FCSTD DOCUMENT  (FreeCAD 0.18R4 (GitTag))
Label: butelka front
License: All rights reserved
LicenseURL: http://en.wikipedia.org/wiki/All_rights_reserved
objects: Sketcher::SketchObject×1, PartDesign::Body×1
note: 2 computed .brp shape members not serialized (recipe doc carries the construction recipe); baked Part::Feature solids carry a one-line shape summary decoded from their .brp

FEATURE [Sketcher::SketchObject] Sketch
  MapMode = 5
  Support = -> [XY_Plane]
  sketch-geometry (321):
    g0: ArcOfCircle CenterX=0 CenterY=58.4018 CenterZ=0 NormalX=0 NormalY=0 NormalZ=1 AngleXU=0 Radius=67 StartAngle=2.08563 EndAngle=4.20019
    g1: LineSegment StartX=-17 StartY=149 StartZ=0 EndX=-16 EndY=149 EndZ=0
    g2: LineSegment StartX=17 StartY=149 StartZ=0 EndX=17 EndY=144.134 EndZ=0
    g3: LineSegment StartX=-17 StartY=144.134 StartZ=0 EndX=-17 EndY=149 EndZ=0
    g4: LineSegment [constr] StartX=-50 StartY=103 StartZ=0 EndX=50 EndY=103 EndZ=0
    g5: LineSegment StartX=32.8364 StartY=0 StartZ=0 EndX=-32.8364 EndY=7.1e-15 EndZ=0
    g6: ArcOfCircle CenterX=0 CenterY=58.4018 CenterZ=0 NormalX=0 NormalY=0 NormalZ=1 AngleXU=0 Radius=67 StartAngle=5.22459 EndAngle=7.33915
    g7: ArcOfCircle CenterX=48.5 CenterY=144.134 CenterZ=0 NormalX=0 NormalY=0 NormalZ=1 AngleXU=0 Radius=31.5 StartAngle=3.14159 EndAngle=4.19756
    g8: ArcOfCircle CenterX=-48.5 CenterY=144.134 CenterZ=0 NormalX=0 NormalY=0 NormalZ=1 AngleXU=0 Radius=31.5 StartAngle=5.22722 EndAngle=6.28319
    g9: LineSegment StartX=-16 StartY=211 StartZ=0 EndX=16 EndY=211 EndZ=0
    g10: LineSegment StartX=16 StartY=211 StartZ=0 EndX=16 EndY=149 EndZ=0
    g11: LineSegment StartX=-16 StartY=149 StartZ=0 EndX=-16 EndY=211 EndZ=0
    g12: LineSegment StartX=16 StartY=149 StartZ=0 EndX=17 EndY=149 EndZ=0
    g13: LineSegment StartX=-80 StartY=-15 StartZ=0 EndX=80 EndY=-15 EndZ=0
    g14: LineSegment StartX=80 StartY=-15 StartZ=0 EndX=80 EndY=10 EndZ=0
    g15: LineSegment StartX=80 StartY=10 StartZ=0 EndX=76.35 EndY=10 EndZ=0
    g16: LineSegment StartX=76.35 StartY=10 StartZ=0 EndX=76.35 EndY=13 EndZ=0
    g17: LineSegment StartX=76.35 StartY=13 StartZ=0 EndX=80 EndY=13 EndZ=0
    g18: LineSegment StartX=80 StartY=13 StartZ=0 EndX=80 EndY=16 EndZ=0
    g19: LineSegment StartX=80 StartY=16 StartZ=0 EndX=76.35 EndY=16 EndZ=0
    g20: LineSegment StartX=76.35 StartY=16 StartZ=0 EndX=76.35 EndY=19 EndZ=0
    g21: LineSegment StartX=76.35 StartY=19 StartZ=0 EndX=80 EndY=19 EndZ=0
    g22: LineSegment StartX=80 StartY=19 StartZ=0 EndX=80 EndY=22 EndZ=0
    g23: LineSegment StartX=80 StartY=22 StartZ=0 EndX=76.35 EndY=22 EndZ=0
    g24: LineSegment StartX=76.35 StartY=22 StartZ=0 EndX=76.35 EndY=25 EndZ=0
    g25: LineSegment StartX=76.35 StartY=25 StartZ=0 EndX=80 EndY=25 EndZ=0
    g26: LineSegment StartX=80 StartY=25 StartZ=0 EndX=80 EndY=28 EndZ=0
    g27: LineSegment StartX=80 StartY=28 StartZ=0 EndX=76.35 EndY=28 EndZ=0
    g28: LineSegment StartX=76.35 StartY=28 StartZ=0 EndX=76.35 EndY=31 EndZ=0
    g29: LineSegment StartX=76.35 StartY=31 StartZ=0 EndX=80 EndY=31 EndZ=0
    g30: LineSegment StartX=80 StartY=31 StartZ=0 EndX=80 EndY=34 EndZ=0
    g31: LineSegment StartX=80 StartY=34 StartZ=0 EndX=76.35 EndY=34 EndZ=0
    g32: LineSegment StartX=76.35 StartY=34 StartZ=0 EndX=76.35 EndY=37 EndZ=0
    g33: LineSegment StartX=76.35 StartY=37 StartZ=0 EndX=80 EndY=37 EndZ=0
    g34: LineSegment StartX=80 StartY=37 StartZ=0 EndX=80 EndY=40 EndZ=0
    g35: LineSegment StartX=80 StartY=40 StartZ=0 EndX=76.35 EndY=40 EndZ=0
    g36: LineSegment StartX=76.35 StartY=40 StartZ=0 EndX=76.35 EndY=43 EndZ=0
    g37: LineSegment StartX=76.35 StartY=43 StartZ=0 EndX=80 EndY=43 EndZ=0
    g38: LineSegment StartX=80 StartY=43 StartZ=0 EndX=80 EndY=46 EndZ=0
    g39: LineSegment StartX=80 StartY=46 StartZ=0 EndX=76.35 EndY=46 EndZ=0
    g40: LineSegment StartX=76.35 StartY=46 StartZ=0 EndX=76.35 EndY=49 EndZ=0
    g41: LineSegment StartX=76.35 StartY=49 StartZ=0 EndX=80 EndY=49 EndZ=0
    g42: LineSegment StartX=80 StartY=49 StartZ=0 EndX=80 EndY=52 EndZ=0
    g43: LineSegment StartX=80 StartY=52 StartZ=0 EndX=76.35 EndY=52 EndZ=0
    g44: LineSegment StartX=76.35 StartY=52 StartZ=0 EndX=76.35 EndY=55 EndZ=0
    g45: LineSegment StartX=76.35 StartY=55 StartZ=0 EndX=80 EndY=55 EndZ=0
    g46: LineSegment StartX=80 StartY=55 StartZ=0 EndX=80 EndY=58 EndZ=0
    g47: LineSegment StartX=80 StartY=58 StartZ=0 EndX=76.35 EndY=58 EndZ=0
    g48: LineSegment StartX=76.35 StartY=58 StartZ=0 EndX=76.35 EndY=61 EndZ=0
    g49: LineSegment StartX=76.35 StartY=61 StartZ=0 EndX=80 EndY=61 EndZ=0
    g50: LineSegment StartX=80 StartY=61 StartZ=0 EndX=80 EndY=64 EndZ=0
    g51: LineSegment StartX=80 StartY=64 StartZ=0 EndX=76.35 EndY=64 EndZ=0
    g52: LineSegment StartX=76.35 StartY=64 StartZ=0 EndX=76.35 EndY=67 EndZ=0
    g53: LineSegment StartX=76.35 StartY=67 StartZ=0 EndX=80 EndY=67 EndZ=0
    g54: LineSegment StartX=80 StartY=67 StartZ=0 EndX=80 EndY=70 EndZ=0
    g55: LineSegment StartX=80 StartY=70 StartZ=0 EndX=76.35 EndY=70 EndZ=0
    g56: LineSegment StartX=76.35 StartY=70 StartZ=0 EndX=76.35 EndY=73 EndZ=0
    g57: LineSegment StartX=76.35 StartY=73 StartZ=0 EndX=80 EndY=73 EndZ=0
    g58: LineSegment StartX=80 StartY=73 StartZ=0 EndX=80 EndY=76 EndZ=0
    g59: LineSegment StartX=80 StartY=76 StartZ=0 EndX=76.35 EndY=76 EndZ=0
    g60: LineSegment StartX=76.35 StartY=76 StartZ=0 EndX=76.35 EndY=79 EndZ=0
    g61: LineSegment StartX=76.35 StartY=79 StartZ=0 EndX=80 EndY=79 EndZ=0
    g62: LineSegment StartX=80 StartY=79 StartZ=0 EndX=80 EndY=82 EndZ=0
    g63: LineSegment StartX=80 StartY=82 StartZ=0 EndX=76.35 EndY=82 EndZ=0
    g64: LineSegment StartX=76.35 StartY=82 StartZ=0 EndX=76.35 EndY=85 EndZ=0
    g65: LineSegment StartX=76.35 StartY=85 StartZ=0 EndX=80 EndY=85 EndZ=0
    g66: LineSegment StartX=80 StartY=85 StartZ=0 EndX=80 EndY=88 EndZ=0
    g67: LineSegment StartX=80 StartY=88 StartZ=0 EndX=76.35 EndY=88 EndZ=0
    g68: LineSegment StartX=76.35 StartY=88 StartZ=0 EndX=76.35 EndY=91 EndZ=0
    g69: LineSegment StartX=76.35 StartY=91 StartZ=0 EndX=80 EndY=91 EndZ=0
    g70: LineSegment StartX=80 StartY=91 StartZ=0 EndX=80 EndY=94 EndZ=0
    g71: LineSegment StartX=80 StartY=94 StartZ=0 EndX=76.35 EndY=94 EndZ=0
    g72: LineSegment StartX=76.35 StartY=94 StartZ=0 EndX=76.35 EndY=97 EndZ=0
    g73: LineSegment StartX=76.35 StartY=97 StartZ=0 EndX=80 EndY=97 EndZ=0
    g74: LineSegment StartX=80 StartY=97 StartZ=0 EndX=80 EndY=100 EndZ=0
    g75: LineSegment StartX=80 StartY=100 StartZ=0 EndX=76.35 EndY=100 EndZ=0
    g76: LineSegment StartX=76.35 StartY=100 StartZ=0 EndX=76.35 EndY=103 EndZ=0
    g77: LineSegment StartX=76.35 StartY=103 StartZ=0 EndX=80 EndY=103 EndZ=0
    g78: LineSegment StartX=80 StartY=103 StartZ=0 EndX=80 EndY=106 EndZ=0
    g79: LineSegment StartX=80 StartY=106 StartZ=0 EndX=76.35 EndY=106 EndZ=0
    g80: LineSegment StartX=76.35 StartY=106 StartZ=0 EndX=76.35 EndY=109 EndZ=0
    g81: LineSegment StartX=76.35 StartY=109 StartZ=0 EndX=80 EndY=109 EndZ=0
    g82: LineSegment StartX=80 StartY=109 StartZ=0 EndX=80 EndY=112 EndZ=0
    g83: LineSegment StartX=80 StartY=112 StartZ=0 EndX=76.35 EndY=112 EndZ=0
    g84: LineSegment StartX=76.35 StartY=112 StartZ=0 EndX=76.35 EndY=115 EndZ=0
    g85: LineSegment StartX=76.35 StartY=115 StartZ=0 EndX=80 EndY=115 EndZ=0
    g86: LineSegment StartX=80 StartY=115 StartZ=0 EndX=80 EndY=118 EndZ=0
    g87: LineSegment StartX=80 StartY=118 StartZ=0 EndX=76.35 EndY=118 EndZ=0
    g88: LineSegment StartX=76.35 StartY=118 StartZ=0 EndX=76.35 EndY=121 EndZ=0
    g89: LineSegment StartX=76.35 StartY=121 StartZ=0 EndX=80 EndY=121 EndZ=0
    g90: LineSegment StartX=80 StartY=121 StartZ=0 EndX=80 EndY=124 EndZ=0
    g91: LineSegment StartX=80 StartY=124 StartZ=0 EndX=76.35 EndY=124 EndZ=0
    g92: LineSegment StartX=76.35 StartY=124 StartZ=0 EndX=76.35 EndY=127 EndZ=0
    g93: LineSegment StartX=76.35 StartY=127 StartZ=0 EndX=80 EndY=127 EndZ=0
    g94: LineSegment StartX=80 StartY=127 StartZ=0 EndX=80 EndY=130 EndZ=0
    g95: LineSegment StartX=80 StartY=130 StartZ=0 EndX=76.35 EndY=130 EndZ=0
    g96: LineSegment StartX=76.35 StartY=130 StartZ=0 EndX=76.35 EndY=133 EndZ=0
    g97: LineSegment StartX=76.35 StartY=133 StartZ=0 EndX=80 EndY=133 EndZ=0
    g98: LineSegment StartX=80 StartY=133 StartZ=0 EndX=80 EndY=136 EndZ=0
    g99: LineSegment StartX=80 StartY=136 StartZ=0 EndX=76.35 EndY=136 EndZ=0
    g100: LineSegment StartX=76.35 StartY=136 StartZ=0 EndX=76.35 EndY=139 EndZ=0
    g101: LineSegment StartX=76.35 StartY=139 StartZ=0 EndX=80 EndY=139 EndZ=0
    g102: LineSegment StartX=80 StartY=139 StartZ=0 EndX=80 EndY=142 EndZ=0
    g103: LineSegment StartX=80 StartY=142 StartZ=0 EndX=76.35 EndY=142 EndZ=0
    g104: LineSegment StartX=76.35 StartY=142 StartZ=0 EndX=76.35 EndY=145 EndZ=0
    g105: LineSegment StartX=76.35 StartY=145 StartZ=0 EndX=80 EndY=145 EndZ=0
    g106: LineSegment StartX=80 StartY=145 StartZ=0 EndX=80 EndY=148 EndZ=0
    g107: LineSegment StartX=80 StartY=148 StartZ=0 EndX=76.35 EndY=148 EndZ=0
    g108: LineSegment StartX=76.35 StartY=148 StartZ=0 EndX=76.35 EndY=151 EndZ=0
    g109: LineSegment StartX=76.35 StartY=151 StartZ=0 EndX=80 EndY=151 EndZ=0
    g110: LineSegment StartX=80 StartY=151 StartZ=0 EndX=80 EndY=154 EndZ=0
    g111: LineSegment StartX=80 StartY=154 StartZ=0 EndX=76.35 EndY=154 EndZ=0
    g112: LineSegment StartX=76.35 StartY=154 StartZ=0 EndX=76.35 EndY=157 EndZ=0
    g113: LineSegment StartX=76.35 StartY=157 StartZ=0 EndX=80 EndY=157 EndZ=0
    g114: LineSegment StartX=80 StartY=157 StartZ=0 EndX=80 EndY=160 EndZ=0
    g115: LineSegment StartX=80 StartY=160 StartZ=0 EndX=76.35 EndY=160 EndZ=0
    g116: LineSegment StartX=76.35 StartY=160 StartZ=0 EndX=76.35 EndY=163 EndZ=0
    g117: LineSegment StartX=76.35 StartY=163 StartZ=0 EndX=80 EndY=163 EndZ=0
    g118: LineSegment StartX=80 StartY=163 StartZ=0 EndX=80 EndY=166 EndZ=0
    g119: LineSegment StartX=80 StartY=166 StartZ=0 EndX=76.35 EndY=166 EndZ=0
    g120: LineSegment StartX=76.35 StartY=166 StartZ=0 EndX=76.35 EndY=169 EndZ=0
    g121: LineSegment StartX=76.35 StartY=169 StartZ=0 EndX=80 EndY=169 EndZ=0
    g122: LineSegment StartX=80 StartY=169 StartZ=0 EndX=80 EndY=172 EndZ=0
    g123: LineSegment StartX=80 StartY=172 StartZ=0 EndX=76.35 EndY=172 EndZ=0
    g124: LineSegment StartX=76.35 StartY=172 StartZ=0 EndX=76.35 EndY=175 EndZ=0
    g125: LineSegment StartX=76.35 StartY=175 StartZ=0 EndX=80 EndY=175 EndZ=0
    g126: LineSegment StartX=80 StartY=175 StartZ=0 EndX=80 EndY=178 EndZ=0
    g127: LineSegment StartX=80 StartY=178 StartZ=0 EndX=76.35 EndY=178 EndZ=0
    g128: LineSegment StartX=76.35 StartY=178 StartZ=0 EndX=76.35 EndY=181 EndZ=0
    g129: LineSegment StartX=76.35 StartY=181 StartZ=0 EndX=80 EndY=181 EndZ=0
    g130: LineSegment StartX=80 StartY=181 StartZ=0 EndX=80 EndY=184 EndZ=0
    g131: LineSegment StartX=80 StartY=184 StartZ=0 EndX=76.35 EndY=184 EndZ=0
    g132: LineSegment StartX=76.35 StartY=184 StartZ=0 EndX=76.35 EndY=187 EndZ=0
    g133: LineSegment StartX=76.35 StartY=187 StartZ=0 EndX=80 EndY=187 EndZ=0
    g134: LineSegment StartX=80 StartY=187 StartZ=0 EndX=80 EndY=190 EndZ=0
    g135: LineSegment StartX=80 StartY=190 StartZ=0 EndX=76.35 EndY=190 EndZ=0
    g136: LineSegment StartX=76.35 StartY=190 StartZ=0 EndX=76.35 EndY=193 EndZ=0
    g137: LineSegment StartX=76.35 StartY=193 StartZ=0 EndX=80 EndY=193 EndZ=0
    g138: LineSegment StartX=80 StartY=193 StartZ=0 EndX=80 EndY=196 EndZ=0
    g139: LineSegment StartX=80 StartY=196 StartZ=0 EndX=76.35 EndY=196 EndZ=0
    g140: LineSegment StartX=76.35 StartY=196 StartZ=0 EndX=76.35 EndY=199 EndZ=0
    g141: LineSegment StartX=76.35 StartY=199 StartZ=0 EndX=80 EndY=199 EndZ=0
    g142: LineSegment StartX=80 StartY=199 StartZ=0 EndX=80 EndY=202 EndZ=0
    g143: LineSegment StartX=80 StartY=202 StartZ=0 EndX=76.35 EndY=202 EndZ=0
    g144: LineSegment StartX=76.35 StartY=202 StartZ=0 EndX=76.35 EndY=205 EndZ=0
    g145: LineSegment StartX=76.35 StartY=205 StartZ=0 EndX=80 EndY=205 EndZ=0
    g146: LineSegment StartX=80 StartY=205 StartZ=0 EndX=80 EndY=208 EndZ=0
    g147: LineSegment StartX=80 StartY=208 StartZ=0 EndX=76.35 EndY=208 EndZ=0
    g148: LineSegment StartX=76.35 StartY=208 StartZ=0 EndX=76.35 EndY=211 EndZ=0
    g149: LineSegment StartX=76.35 StartY=211 StartZ=0 EndX=80 EndY=211 EndZ=0
    g150: LineSegment StartX=80 StartY=211 StartZ=0 EndX=80 EndY=214 EndZ=0
    g151: LineSegment StartX=80 StartY=214 StartZ=0 EndX=76.35 EndY=214 EndZ=0
    g152: LineSegment StartX=76.35 StartY=214 StartZ=0 EndX=76.35 EndY=217 EndZ=0
    g153: LineSegment StartX=76.35 StartY=217 StartZ=0 EndX=80 EndY=217 EndZ=0
    g154: LineSegment StartX=80 StartY=217 StartZ=0 EndX=80 EndY=220 EndZ=0
    g155: LineSegment StartX=80 StartY=220 StartZ=0 EndX=76.35 EndY=220 EndZ=0
    g156: LineSegment StartX=76.35 StartY=220 StartZ=0 EndX=76.35 EndY=223 EndZ=0
    g157: LineSegment StartX=76.35 StartY=223 StartZ=0 EndX=80 EndY=223 EndZ=0
    g158: LineSegment StartX=80 StartY=223 StartZ=0 EndX=80 EndY=226 EndZ=0
    g159: LineSegment StartX=80 StartY=226 StartZ=0 EndX=76.35 EndY=226 EndZ=0
    g160: LineSegment StartX=76.35 StartY=226 StartZ=0 EndX=76.35 EndY=229 EndZ=0
    g161: LineSegment StartX=76.35 StartY=229 StartZ=0 EndX=80 EndY=229 EndZ=0
    g162: LineSegment StartX=80 StartY=229 StartZ=0 EndX=80 EndY=232 EndZ=0
    g163: LineSegment StartX=80 StartY=232 StartZ=0 EndX=76.35 EndY=232 EndZ=0
    g164: LineSegment StartX=76.35 StartY=232 StartZ=0 EndX=76.35 EndY=235 EndZ=0
    g165: LineSegment StartX=76.35 StartY=235 StartZ=0 EndX=80 EndY=235 EndZ=0
    g166: LineSegment StartX=80 StartY=235 StartZ=0 EndX=80 EndY=260 EndZ=0
    g167: LineSegment StartX=80 StartY=260 StartZ=0 EndX=-80 EndY=260 EndZ=0
    g168: LineSegment StartX=-80 StartY=260 StartZ=0 EndX=-80 EndY=235 EndZ=0
    g169: LineSegment StartX=-80 StartY=235 StartZ=0 EndX=-76.35 EndY=235 EndZ=0
    g170: LineSegment StartX=-76.35 StartY=235 StartZ=0 EndX=-76.35 EndY=232 EndZ=0
    g171: LineSegment StartX=-76.35 StartY=232 StartZ=0 EndX=-80 EndY=232 EndZ=0
    g172: LineSegment StartX=-80 StartY=232 StartZ=0 EndX=-80 EndY=229 EndZ=0
    g173: LineSegment StartX=-80 StartY=229 StartZ=0 EndX=-76.35 EndY=229 EndZ=0
    g174: LineSegment StartX=-76.35 StartY=229 StartZ=0 EndX=-76.35 EndY=226 EndZ=0
    g175: LineSegment StartX=-76.35 StartY=226 StartZ=0 EndX=-80 EndY=226 EndZ=0
    g176: LineSegment StartX=-80 StartY=226 StartZ=0 EndX=-80 EndY=223 EndZ=0
    g177: LineSegment StartX=-80 StartY=223 StartZ=0 EndX=-76.35 EndY=223 EndZ=0
    g178: LineSegment StartX=-76.35 StartY=223 StartZ=0 EndX=-76.35 EndY=220 EndZ=0
    g179: LineSegment StartX=-76.35 StartY=220 StartZ=0 EndX=-80 EndY=220 EndZ=0
    g180: LineSegment StartX=-80 StartY=220 StartZ=0 EndX=-80 EndY=217 EndZ=0
    g181: LineSegment StartX=-80 StartY=217 StartZ=0 EndX=-76.35 EndY=217 EndZ=0
    g182: LineSegment StartX=-76.35 StartY=217 StartZ=0 EndX=-76.35 EndY=214 EndZ=0
    g183: LineSegment StartX=-76.35 StartY=214 StartZ=0 EndX=-80 EndY=214 EndZ=0
    g184: LineSegment StartX=-80 StartY=214 StartZ=0 EndX=-80 EndY=211 EndZ=0
    g185: LineSegment StartX=-80 StartY=211 StartZ=0 EndX=-76.35 EndY=211 EndZ=0
    g186: LineSegment StartX=-76.35 StartY=211 StartZ=0 EndX=-76.35 EndY=208 EndZ=0
    g187: LineSegment StartX=-76.35 StartY=208 StartZ=0 EndX=-80 EndY=208 EndZ=0
    g188: LineSegment StartX=-80 StartY=208 StartZ=0 EndX=-80 EndY=205 EndZ=0
    g189: LineSegment StartX=-80 StartY=205 StartZ=0 EndX=-76.35 EndY=205 EndZ=0
    g190: LineSegment StartX=-76.35 StartY=205 StartZ=0 EndX=-76.35 EndY=202 EndZ=0
    g191: LineSegment StartX=-76.35 StartY=202 StartZ=0 EndX=-80 EndY=202 EndZ=0
    g192: LineSegment StartX=-80 StartY=202 StartZ=0 EndX=-80 EndY=199 EndZ=0
    g193: LineSegment StartX=-80 StartY=199 StartZ=0 EndX=-76.35 EndY=199 EndZ=0
    g194: LineSegment StartX=-76.35 StartY=199 StartZ=0 EndX=-76.35 EndY=196 EndZ=0
    g195: LineSegment StartX=-76.35 StartY=196 StartZ=0 EndX=-80 EndY=196 EndZ=0
    g196: LineSegment StartX=-80 StartY=196 StartZ=0 EndX=-80 EndY=193 EndZ=0
    g197: LineSegment StartX=-80 StartY=193 StartZ=0 EndX=-76.35 EndY=193 EndZ=0
    g198: LineSegment StartX=-76.35 StartY=193 StartZ=0 EndX=-76.35 EndY=190 EndZ=0
    g199: LineSegment StartX=-76.35 StartY=190 StartZ=0 EndX=-80 EndY=190 EndZ=0
    g200: LineSegment StartX=-80 StartY=190 StartZ=0 EndX=-80 EndY=187 EndZ=0
    g201: LineSegment StartX=-80 StartY=187 StartZ=0 EndX=-76.35 EndY=187 EndZ=0
    g202: LineSegment StartX=-76.35 StartY=187 StartZ=0 EndX=-76.35 EndY=184 EndZ=0
    g203: LineSegment StartX=-76.35 StartY=184 StartZ=0 EndX=-80 EndY=184 EndZ=0
    g204: LineSegment StartX=-80 StartY=184 StartZ=0 EndX=-80 EndY=181 EndZ=0
    g205: LineSegment StartX=-80 StartY=181 StartZ=0 EndX=-76.35 EndY=181 EndZ=0
    g206: LineSegment StartX=-76.35 StartY=181 StartZ=0 EndX=-76.35 EndY=178 EndZ=0
    g207: LineSegment StartX=-76.35 StartY=178 StartZ=0 EndX=-80 EndY=178 EndZ=0
    g208: LineSegment StartX=-80 StartY=178 StartZ=0 EndX=-80 EndY=175 EndZ=0
    g209: LineSegment StartX=-80 StartY=175 StartZ=0 EndX=-76.35 EndY=175 EndZ=0
    g210: LineSegment StartX=-76.35 StartY=175 StartZ=0 EndX=-76.35 EndY=172 EndZ=0
    g211: LineSegment StartX=-76.35 StartY=172 StartZ=0 EndX=-80 EndY=172 EndZ=0
    g212: LineSegment StartX=-80 StartY=172 StartZ=0 EndX=-80 EndY=169 EndZ=0
    g213: LineSegment StartX=-80 StartY=169 StartZ=0 EndX=-76.35 EndY=169 EndZ=0
    g214: LineSegment StartX=-76.35 StartY=169 StartZ=0 EndX=-76.35 EndY=166 EndZ=0
    g215: LineSegment StartX=-76.35 StartY=166 StartZ=0 EndX=-80 EndY=166 EndZ=0
    g216: LineSegment StartX=-80 StartY=166 StartZ=0 EndX=-80 EndY=163 EndZ=0
    g217: LineSegment StartX=-80 StartY=163 StartZ=0 EndX=-76.35 EndY=163 EndZ=0
    g218: LineSegment StartX=-76.35 StartY=163 StartZ=0 EndX=-76.35 EndY=160 EndZ=0
    g219: LineSegment StartX=-76.35 StartY=160 StartZ=0 EndX=-80 EndY=160 EndZ=0
    g220: LineSegment StartX=-80 StartY=160 StartZ=0 EndX=-80 EndY=157 EndZ=0
    g221: LineSegment StartX=-80 StartY=157 StartZ=0 EndX=-76.35 EndY=157 EndZ=0
    g222: LineSegment StartX=-76.35 StartY=157 StartZ=0 EndX=-76.35 EndY=154 EndZ=0
    g223: LineSegment StartX=-76.35 StartY=154 StartZ=0 EndX=-80 EndY=154 EndZ=0
    g224: LineSegment StartX=-80 StartY=154 StartZ=0 EndX=-80 EndY=151 EndZ=0
    g225: LineSegment StartX=-80 StartY=151 StartZ=0 EndX=-76.35 EndY=151 EndZ=0
    g226: LineSegment StartX=-76.35 StartY=151 StartZ=0 EndX=-76.35 EndY=148 EndZ=0
    g227: LineSegment StartX=-76.35 StartY=148 StartZ=0 EndX=-80 EndY=148 EndZ=0
    g228: LineSegment StartX=-80 StartY=148 StartZ=0 EndX=-80 EndY=145 EndZ=0
    g229: LineSegment StartX=-80 StartY=145 StartZ=0 EndX=-76.35 EndY=145 EndZ=0
    g230: LineSegment StartX=-76.35 StartY=145 StartZ=0 EndX=-76.35 EndY=142 EndZ=0
    g231: LineSegment StartX=-76.35 StartY=142 StartZ=0 EndX=-80 EndY=142 EndZ=0
    g232: LineSegment StartX=-80 StartY=142 StartZ=0 EndX=-80 EndY=139 EndZ=0
    g233: LineSegment StartX=-80 StartY=139 StartZ=0 EndX=-76.35 EndY=139 EndZ=0
    g234: LineSegment StartX=-76.35 StartY=139 StartZ=0 EndX=-76.35 EndY=136 EndZ=0
    g235: LineSegment StartX=-76.35 StartY=136 StartZ=0 EndX=-80 EndY=136 EndZ=0
    g236: LineSegment StartX=-80 StartY=136 StartZ=0 EndX=-80 EndY=133 EndZ=0
    g237: LineSegment StartX=-80 StartY=133 StartZ=0 EndX=-76.35 EndY=133 EndZ=0
    g238: LineSegment StartX=-76.35 StartY=133 StartZ=0 EndX=-76.35 EndY=130 EndZ=0
    g239: LineSegment StartX=-76.35 StartY=130 StartZ=0 EndX=-80 EndY=130 EndZ=0
    g240: LineSegment StartX=-80 StartY=130 StartZ=0 EndX=-80 EndY=127 EndZ=0
    g241: LineSegment StartX=-80 StartY=127 StartZ=0 EndX=-76.35 EndY=127 EndZ=0
    g242: LineSegment StartX=-76.35 StartY=127 StartZ=0 EndX=-76.35 EndY=124 EndZ=0
    g243: LineSegment StartX=-76.35 StartY=124 StartZ=0 EndX=-80 EndY=124 EndZ=0
    g244: LineSegment StartX=-80 StartY=124 StartZ=0 EndX=-80 EndY=121 EndZ=0
    g245: LineSegment StartX=-80 StartY=121 StartZ=0 EndX=-76.35 EndY=121 EndZ=0
    g246: LineSegment StartX=-76.35 StartY=121 StartZ=0 EndX=-76.35 EndY=118 EndZ=0
    g247: LineSegment StartX=-76.35 StartY=118 StartZ=0 EndX=-80 EndY=118 EndZ=0
    g248: LineSegment StartX=-80 StartY=118 StartZ=0 EndX=-80 EndY=115 EndZ=0
    g249: LineSegment StartX=-80 StartY=115 StartZ=0 EndX=-76.35 EndY=115 EndZ=0
    g250: LineSegment StartX=-76.35 StartY=115 StartZ=0 EndX=-76.35 EndY=112 EndZ=0
    g251: LineSegment StartX=-76.35 StartY=112 StartZ=0 EndX=-80 EndY=112 EndZ=0
    g252: LineSegment StartX=-80 StartY=112 StartZ=0 EndX=-80 EndY=109 EndZ=0
    g253: LineSegment StartX=-80 StartY=109 StartZ=0 EndX=-76.35 EndY=109 EndZ=0
    g254: LineSegment StartX=-76.35 StartY=109 StartZ=0 EndX=-76.35 EndY=106 EndZ=0
    g255: LineSegment StartX=-76.35 StartY=106 StartZ=0 EndX=-80 EndY=106 EndZ=0
    g256: LineSegment StartX=-80 StartY=106 StartZ=0 EndX=-80 EndY=103 EndZ=0
    g257: LineSegment StartX=-80 StartY=103 StartZ=0 EndX=-76.35 EndY=103 EndZ=0
    g258: LineSegment StartX=-76.35 StartY=103 StartZ=0 EndX=-76.35 EndY=100 EndZ=0
    g259: LineSegment StartX=-76.35 StartY=100 StartZ=0 EndX=-80 EndY=100 EndZ=0
    g260: LineSegment StartX=-80 StartY=100 StartZ=0 EndX=-80 EndY=97 EndZ=0
    g261: LineSegment StartX=-80 StartY=97 StartZ=0 EndX=-76.35 EndY=97 EndZ=0
    g262: LineSegment StartX=-76.35 StartY=97 StartZ=0 EndX=-76.35 EndY=94 EndZ=0
    g263: LineSegment StartX=-76.35 StartY=94 StartZ=0 EndX=-80 EndY=94 EndZ=0
    g264: LineSegment StartX=-80 StartY=94 StartZ=0 EndX=-80 EndY=91 EndZ=0
    g265: LineSegment StartX=-80 StartY=91 StartZ=0 EndX=-76.35 EndY=91 EndZ=0
    g266: LineSegment StartX=-76.35 StartY=91 StartZ=0 EndX=-76.35 EndY=88 EndZ=0
    g267: LineSegment StartX=-76.35 StartY=88 StartZ=0 EndX=-80 EndY=88 EndZ=0
    g268: LineSegment StartX=-80 StartY=88 StartZ=0 EndX=-80 EndY=85 EndZ=0
    g269: LineSegment StartX=-80 StartY=85 StartZ=0 EndX=-76.35 EndY=85 EndZ=0
    g270: LineSegment StartX=-76.35 StartY=85 StartZ=0 EndX=-76.35 EndY=82 EndZ=0
    g271: LineSegment StartX=-76.35 StartY=82 StartZ=0 EndX=-80 EndY=82 EndZ=0
    g272: LineSegment StartX=-80 StartY=82 StartZ=0 EndX=-80 EndY=79 EndZ=0
    g273: LineSegment StartX=-80 StartY=79 StartZ=0 EndX=-76.35 EndY=79 EndZ=0
    g274: LineSegment StartX=-76.35 StartY=79 StartZ=0 EndX=-76.35 EndY=76 EndZ=0
    g275: LineSegment StartX=-76.35 StartY=76 StartZ=0 EndX=-80 EndY=76 EndZ=0
    g276: LineSegment StartX=-80 StartY=76 StartZ=0 EndX=-80 EndY=73 EndZ=0
    g277: LineSegment StartX=-80 StartY=73 StartZ=0 EndX=-76.35 EndY=73 EndZ=0
    g278: LineSegment StartX=-76.35 StartY=73 StartZ=0 EndX=-76.35 EndY=70 EndZ=0
    g279: LineSegment StartX=-76.35 StartY=70 StartZ=0 EndX=-80 EndY=70 EndZ=0
    g280: LineSegment StartX=-80 StartY=70 StartZ=0 EndX=-80 EndY=67 EndZ=0
    g281: LineSegment StartX=-80 StartY=67 StartZ=0 EndX=-76.35 EndY=67 EndZ=0
    g282: LineSegment StartX=-76.35 StartY=67 StartZ=0 EndX=-76.35 EndY=64 EndZ=0
    g283: LineSegment StartX=-76.35 StartY=64 StartZ=0 EndX=-80 EndY=64 EndZ=0
    g284: LineSegment StartX=-80 StartY=64 StartZ=0 EndX=-80 EndY=61 EndZ=0
    g285: LineSegment StartX=-80 StartY=61 StartZ=0 EndX=-76.35 EndY=61 EndZ=0
    g286: LineSegment StartX=-76.35 StartY=61 StartZ=0 EndX=-76.35 EndY=58 EndZ=0
    g287: LineSegment StartX=-76.35 StartY=58 StartZ=0 EndX=-80 EndY=58 EndZ=0
    g288: LineSegment StartX=-80 StartY=58 StartZ=0 EndX=-80 EndY=55 EndZ=0
    g289: LineSegment StartX=-80 StartY=55 StartZ=0 EndX=-76.35 EndY=55 EndZ=0
    g290: LineSegment StartX=-76.35 StartY=55 StartZ=0 EndX=-76.35 EndY=52 EndZ=0
    g291: LineSegment StartX=-76.35 StartY=52 StartZ=0 EndX=-80 EndY=52 EndZ=0
    g292: LineSegment StartX=-80 StartY=52 StartZ=0 EndX=-80 EndY=49 EndZ=0
    g293: LineSegment StartX=-80 StartY=49 StartZ=0 EndX=-76.35 EndY=49 EndZ=0
    g294: LineSegment StartX=-76.35 StartY=49 StartZ=0 EndX=-76.35 EndY=46 EndZ=0
    g295: LineSegment StartX=-76.35 StartY=46 StartZ=0 EndX=-80 EndY=46 EndZ=0
    g296: LineSegment StartX=-80 StartY=46 StartZ=0 EndX=-80 EndY=43 EndZ=0
    g297: LineSegment StartX=-80 StartY=43 StartZ=0 EndX=-76.35 EndY=43 EndZ=0
    g298: LineSegment StartX=-76.35 StartY=43 StartZ=0 EndX=-76.35 EndY=40 EndZ=0
    g299: LineSegment StartX=-76.35 StartY=40 StartZ=0 EndX=-80 EndY=40 EndZ=0
    g300: LineSegment StartX=-80 StartY=40 StartZ=0 EndX=-80 EndY=37 EndZ=0
    g301: LineSegment StartX=-80 StartY=37 StartZ=0 EndX=-76.35 EndY=37 EndZ=0
    g302: LineSegment StartX=-76.35 StartY=37 StartZ=0 EndX=-76.35 EndY=34 EndZ=0
    g303: LineSegment StartX=-76.35 StartY=34 StartZ=0 EndX=-80 EndY=34 EndZ=0
    g304: LineSegment StartX=-80 StartY=34 StartZ=0 EndX=-80 EndY=31 EndZ=0
    g305: LineSegment StartX=-80 StartY=31 StartZ=0 EndX=-76.35 EndY=31 EndZ=0
    g306: LineSegment StartX=-76.35 StartY=31 StartZ=0 EndX=-76.35 EndY=28 EndZ=0
    g307: LineSegment StartX=-76.35 StartY=28 StartZ=0 EndX=-80 EndY=28 EndZ=0
    g308: LineSegment StartX=-80 StartY=28 StartZ=0 EndX=-80 EndY=25 EndZ=0
    g309: LineSegment StartX=-80 StartY=25 StartZ=0 EndX=-76.35 EndY=25 EndZ=0
    g310: LineSegment StartX=-76.35 StartY=25 StartZ=0 EndX=-76.35 EndY=22 EndZ=0
    g311: LineSegment StartX=-76.35 StartY=22 StartZ=0 EndX=-80 EndY=22 EndZ=0
    g312: LineSegment StartX=-80 StartY=22 StartZ=0 EndX=-80 EndY=19 EndZ=0
    g313: LineSegment StartX=-80 StartY=19 StartZ=0 EndX=-76.35 EndY=19 EndZ=0
    g314: LineSegment StartX=-76.35 StartY=19 StartZ=0 EndX=-76.35 EndY=16 EndZ=0
    g315: LineSegment StartX=-76.35 StartY=16 StartZ=0 EndX=-80 EndY=16 EndZ=0
    g316: LineSegment StartX=-80 StartY=16 StartZ=0 EndX=-80 EndY=13 EndZ=0
    g317: LineSegment StartX=-80 StartY=13 StartZ=0 EndX=-76.35 EndY=13 EndZ=0
    g318: LineSegment StartX=-76.35 StartY=13 StartZ=0 EndX=-76.35 EndY=10 EndZ=0
    g319: LineSegment StartX=-76.35 StartY=10 StartZ=0 EndX=-80 EndY=10 EndZ=0
    g320: LineSegment StartX=-80 StartY=10 StartZ=0 EndX=-80 EndY=-15 EndZ=0
  constraints (42):
    c: Coincident(g12,g2)
    c: Coincident(g3,g1)
    c: Vertical(g2)
    c: Vertical(g3)
    c: DistanceY(g1) = 149
    c: Symmetric(g1,g12,g-2)
    c: PointOnObject(g4,g0)
    c: PointOnObject(g4,g0)
    c: Horizontal(g4)
    c: Distance(g4) = 100
    c: DistanceY(g4) = 103
    c: Equal(g0,g6)
    c: Coincident(g0,g5)
    c: Coincident(g6,g5)
    c: Coincident(g0,g6)
    c: Vertical(g0)
    c: PointOnObject(g0,g-2)
    c: PointOnObject(g0,g-1)
    c: PointOnObject(g5,g-1)
    c: Tangent(g3,g8)
    c: Tangent(g0,g8)
    c: Tangent(g7,g2)
    c: Tangent(g6,g7)
    c: Diameter(g7) = 63
    c: Diameter(g8) = 63
    c: Coincident(g2,g7)
    c: Coincident(g6,g7)
    c: Coincident(g3,g8)
    c: Coincident(g0,g8)
    c: Coincident(g9,g10)
    c: Coincident(g11,g9)
    c: Horizontal(g9)
    c: Vertical(g10)
    c: Vertical(g11)
    c: Distance(g9) = 32
    c: DistanceY(g9) = 211
    c: Coincident(g1,g11)
    c: PointOnObject(g12,g10)
    c: Tangent(g1,g12)
    c: Distance(g1,g2) = 34
    c: Symmetric(g10,g1,g-2)
    c: Vertical(g0)
FEATURE [PartDesign::Body] Body
  Group = -> [Sketch]
  Origin = -> Origin
